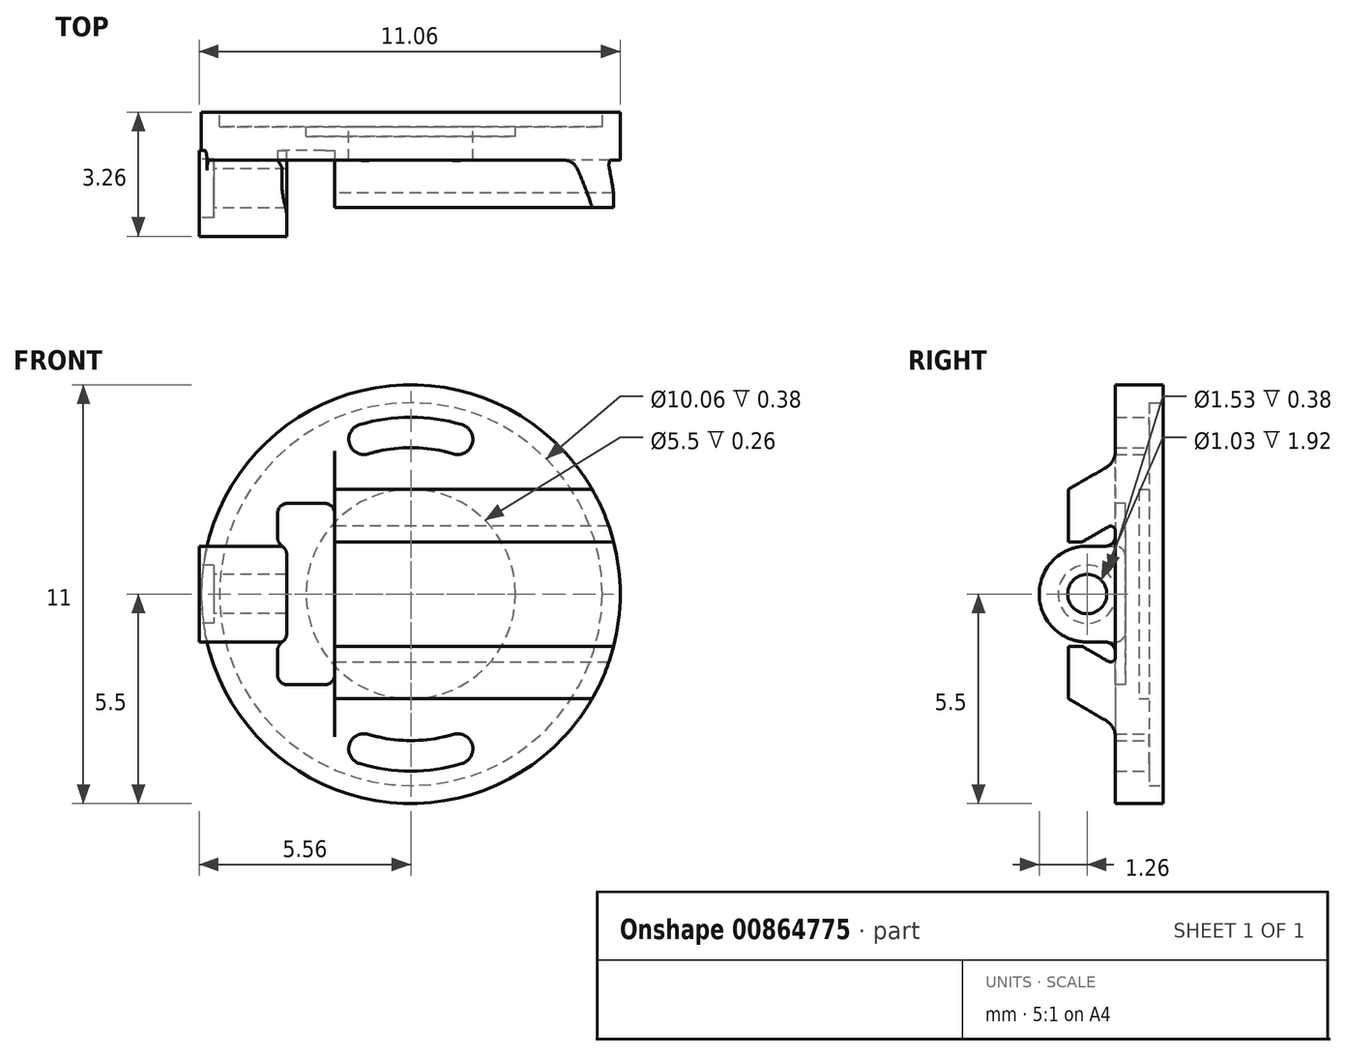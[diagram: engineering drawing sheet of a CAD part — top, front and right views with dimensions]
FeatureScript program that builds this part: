
annotation { "Feature Type Name" : "Feature", "Feature Type Description" : "" }
export const myFeature = defineFeature(function(context is Context, id is Id, definition is map)
    precondition{}
    {
        {
            var Q0;
            Q0=qCreatedBy(makeId("Front.planeOp"),FACE);
            var sketch = newSketch(context, id + "F0", { "sketchPlane" : qUnion([Q0])});
            skCircle(sketch, "E0", {"center": v(0, 0) * mm, "radius": 5.5 * mm});
            skSolve(sketch);
        }
        {
            var Q0;
            Q0 = qSketchRegion(id + "F0", true);
            extrude(context, id + "F1", {"entities" : qUnion([Q0]), "depth" : 1.26 * mm, "offsetDistance" : 25.4 * mm});
        }
        {
            var Q0;
            Q0=makeQuery(id+"F1.opExtrude","CAP_FACE",FACE,{"disambiguationData":[OSD([sQuery(id+"F0.wireOp",EDGE,"E0")])],"isStart":true});
            var sketch = newSketch(context, id + "F2", { "sketchPlane" : qUnion([Q0])});
            skCircle(sketch, "E1", {"center": v(0, 0) * mm, "radius": 5.03 * mm});
            skSolve(sketch);
        }
        {
            var Q0;
            Q0 = qSketchRegion(id + "F2", true);
            extrude(context, id + "F3", {"entities" : qUnion([Q0]), "operationType" : NewBodyOperationType.REMOVE, "oppositeDirection" : true, "depth" : .38 * mm, "offsetDistance" : 25.4 * mm});
        }
        {
            var Q0;
            Q0=makeQuery(id+"F3.boolean.opBoolean","COPY",FACE,{"derivedFrom":makeQuery(id+"F3.opExtrude","CAP_FACE",FACE,{"disambiguationData":[OSD([sQuery(id+"F2.wireOp",EDGE,"E1")])],"isStart":false})});
            var sketch = newSketch(context, id + "F4", { "sketchPlane" : qUnion([Q0])});
            skCircle(sketch, "E2", {"center": v(0, 0) * mm, "radius": 2.75 * mm});
            skSolve(sketch);
        }
        {
            var Q0;
            Q0 = qSketchRegion(id + "F4", true);
            extrude(context, id + "F5", {"entities" : qUnion([Q0]), "operationType" : NewBodyOperationType.REMOVE, "oppositeDirection" : true, "depth" : .26 * mm, "offsetDistance" : 25.4 * mm});
        }
        {
            var Q0;
            Q0=makeQuery(id+"F1.opExtrude","CAP_FACE",FACE,{"disambiguationData":[OSD([sQuery(id+"F0.wireOp",EDGE,"E0")])],"isStart":false});
            var sketch = newSketch(context, id + "F6", { "sketchPlane" : qUnion([Q0])});
            skArc(sketch, "E3", {"start": v(1.23, 4.07) * mm, "mid": v(0, 4.25) * mm, "end": v(-1.23, 4.07) * mm, "construction": true});
            skArc(sketch, "E4", {"start": v(1.11, 3.69) * mm, "mid": v(0, 3.85) * mm, "end": v(-1.11, 3.69) * mm});
            skArc(sketch, "E5", {"start": v(1.35, 4.45) * mm, "mid": v(0, 4.65) * mm, "end": v(-1.35, 4.45) * mm});
            skArc(sketch, "E6", {"start": v(-1.11, -3.69) * mm, "mid": v(0, -3.85) * mm, "end": v(1.11, -3.69) * mm});
            skArc(sketch, "E7", {"start": v(-1.35, -4.45) * mm, "mid": v(0, -4.65) * mm, "end": v(1.35, -4.45) * mm});
            skArc(sketch, "E8.trimOffspring", {"start": v(-1.23, -4.07) * mm, "mid": v(0, -4.25) * mm, "end": v(1.23, -4.07) * mm, "construction": true});
            skArc(sketch, "E9", {"start": v(-1.35, 4.45) * mm, "mid": v(-1.61, 3.95) * mm, "end": v(-1.11, 3.69) * mm});
            skArc(sketch, "E10", {"start": v(1.11, 3.69) * mm, "mid": v(1.61, 3.95) * mm, "end": v(1.35, 4.45) * mm});
            skArc(sketch, "E11", {"start": v(1.35, -4.45) * mm, "mid": v(1.61, -3.95) * mm, "end": v(1.11, -3.69) * mm});
            skArc(sketch, "E12", {"start": v(-1.11, -3.69) * mm, "mid": v(-1.61, -3.95) * mm, "end": v(-1.35, -4.45) * mm});
            skLineSegment(sketch, "E13", {"start": v(0, 0) * mm, "end": v(0, 2.82) * mm, "construction": true});
            skSolve(sketch);
        }
        {
            var Q0;
            Q0 = qSketchRegion(id + "F6", true);
            extrude(context, id + "F7", {"entities" : qUnion([Q0]), "operationType" : NewBodyOperationType.REMOVE, "endBound" : BoundingType.SYMMETRIC, "depth" : 15 * mm, "offsetDistance" : 25.4 * mm});
        }
        {
            var Q0;
            Q0=makeQuery(id+"F1.opExtrude","CAP_FACE",FACE,{"disambiguationData":[OSD([sQuery(id+"F0.wireOp",EDGE,"E0")])],"isStart":false});
            var sketch = newSketch(context, id + "F8", { "sketchPlane" : qUnion([Q0])});
            skLineSegment(sketch, "E14", {"start": v(-2, 2.38) * mm, "end": v(-2, -2.38) * mm});
            skLineSegment(sketch, "E15", {"start": v(-2, -2.38) * mm, "end": v(-3.5, -2.38) * mm});
            skLineSegment(sketch, "E16", {"start": v(-3.5, -2.38) * mm, "end": v(-3.5, -1.48) * mm});
            skLineSegment(sketch, "E17", {"start": v(-3.26, -1.04) * mm, "end": v(-3.26, 1.04) * mm});
            skLineSegment(sketch, "E18", {"start": v(-3.5, 1.48) * mm, "end": v(-3.5, 2.38) * mm});
            skLineSegment(sketch, "E19", {"start": v(-3.5, 2.38) * mm, "end": v(-2, 2.38) * mm});
            skArc(sketch, "E20", {"start": v(-3.26, 1.04) * mm, "mid": v(-3.3, 1.17) * mm, "end": v(-3.38, 1.26) * mm});
            skArc(sketch, "E21", {"start": v(-3.5, 1.48) * mm, "mid": v(-3.47, 1.35) * mm, "end": v(-3.38, 1.26) * mm});
            skArc(sketch, "E22", {"start": v(-3.38, -1.26) * mm, "mid": v(-3.3, -1.17) * mm, "end": v(-3.26, -1.04) * mm});
            skArc(sketch, "E23", {"start": v(-3.38, -1.26) * mm, "mid": v(-3.47, -1.35) * mm, "end": v(-3.5, -1.48) * mm});
            skSolve(sketch);
        }
        {
            var Q0;
            Q0 = qSketchRegion(id + "F8", true);
            extrude(context, id + "F9", {"entities" : qUnion([Q0]), "operationType" : NewBodyOperationType.REMOVE, "oppositeDirection" : true, "depth" : .26 * mm, "offsetDistance" : 25.4 * mm});
        }
        {
            var Q0;
            Q0=makeQuery(id+"F9.boolean.opBoolean","COPY",EDGE,{"derivedFrom":makeQuery(id+"F9.opExtrude","SWEPT_EDGE",EDGE,{"disambiguationData":[OSD([sQuery(id+"F8.wireOp",EDGE,"E14"),sQuery(id+"F8.wireOp",EDGE,"E19")])]})});
            var Q1;
            Q1=makeQuery(id+"F9.boolean.opBoolean","COPY",EDGE,{"derivedFrom":makeQuery(id+"F9.opExtrude","SWEPT_EDGE",EDGE,{"disambiguationData":[OSD([sQuery(id+"F8.wireOp",EDGE,"E18"),sQuery(id+"F8.wireOp",EDGE,"E19")])]})});
            var Q2;
            Q2=makeQuery(id+"F9.boolean.opBoolean","COPY",EDGE,{"derivedFrom":makeQuery(id+"F9.opExtrude","SWEPT_EDGE",EDGE,{"disambiguationData":[OSD([sQuery(id+"F8.wireOp",EDGE,"E15"),sQuery(id+"F8.wireOp",EDGE,"E16")])]})});
            var Q3;
            Q3=makeQuery(id+"F9.boolean.opBoolean","COPY",EDGE,{"derivedFrom":makeQuery(id+"F9.opExtrude","SWEPT_EDGE",EDGE,{"disambiguationData":[OSD([sQuery(id+"F8.wireOp",EDGE,"E14"),sQuery(id+"F8.wireOp",EDGE,"E15")])]})});
            fillet(context, id + "F10", {"entities" : qUnion([Q0, Q1, Q2, Q3]), "radius" : .26 * mm, "tangentPropagation" : true, "allowEdgeOverflow" : false});
        }
        {
            var Q0;
            Q0=makeQuery(id+"F9.boolean.opBoolean","COPY",FACE,{"derivedFrom":makeQuery(id+"F9.opExtrude","SWEPT_FACE",FACE,{"disambiguationData":[OSD([sQuery(id+"F8.wireOp",EDGE,"E17")])]})});
            cPlane(context, id + "F11", {"entities" : qUnion([Q0]), "cplaneType" : CPlaneType.OFFSET, "offset" : 2.3 * mm, "oppositeDirection" : true, "width" : 152.4 * mm, "height" : 152.4 * mm});
        }
        {
            var Q0;
            Q0=qCreatedBy(id+"F11.planeOp",FACE);
            var sketch = newSketch(context, id + "F12", { "sketchPlane" : qUnion([Q0])});
            skLineSegment(sketch, "E24", {"start": v(-1, 1.26) * mm, "end": v(-2, 1.26) * mm});
            skLineSegment(sketch, "E25", {"start": v(-2, -1.26) * mm, "end": v(-1, -1.26) * mm});
            skArc(sketch, "E26", {"start": v(-2, 1.26) * mm, "mid": v(-3.26, 0) * mm, "end": v(-2, -1.26) * mm});
            skLineSegment(sketch, "E27", {"start": v(-1, 1.26) * mm, "end": v(-1, -1.26) * mm});
            skSolve(sketch);
        }
        {
            var Q0;
            {var subQ1=sQuery(id+"F12.wireOp",EDGE,"E24");Q0=makeQuery(id+"F12.imprint","IMPRINT",FACE,{"disambiguationData":[TD([[makeQuery(id+"F12.imprint","IMPRINT",EDGE,{"derivedFrom":subQ1}),1.0]])]});}
            var Q1;
            Q1=makeQuery(id+"F9.boolean.opBoolean","COPY",FACE,{"derivedFrom":makeQuery(id+"F9.opExtrude","SWEPT_FACE",FACE,{"disambiguationData":[OSD([sQuery(id+"F8.wireOp",EDGE,"E17")])]})});
            extrude(context, id + "F13", {"entities" : qUnion([Q0]), "operationType" : NewBodyOperationType.ADD, "endBound" : BoundingType.UP_TO_SURFACE, "depth" : 25.4 * mm, "endBoundEntityFace" : qUnion([Q1]), "offsetDistance" : 25.4 * mm});
        }
        {
            var Q0;
            Q0=makeQuery(id+"F13.opExtrude","CAP_FACE",FACE,{"disambiguationData":[OSD([sQuery(id+"F12.wireOp",EDGE,"E24"),sQuery(id+"F12.wireOp",EDGE,"E25"),sQuery(id+"F12.wireOp",EDGE,"ZlhiLMFL-Lc4S-4lp4-7yYM-Jzgoso8IJn7b"),sQuery(id+"F12.wireOp",EDGE,"E26")])],"isStart":true});
            var sketch = newSketch(context, id + "F14", { "sketchPlane" : qUnion([Q0])});
            skCircle(sketch, "E28", {"center": v(2, 0) * mm, "radius": 0.77 * mm});
            skSolve(sketch);
        }
        {
            var Q0;
            Q0 = qSketchRegion(id + "F14", true);
            extrude(context, id + "F15", {"entities" : qUnion([Q0]), "operationType" : NewBodyOperationType.REMOVE, "oppositeDirection" : true, "depth" : .38 * mm, "offsetDistance" : 25.4 * mm});
        }
        {
            var Q0;
            Q0=makeQuery(id+"F15.boolean.opBoolean","COPY",FACE,{"derivedFrom":makeQuery(id+"F15.opExtrude","CAP_FACE",FACE,{"disambiguationData":[OSD([sQuery(id+"F14.wireOp",EDGE,"E28")])],"isStart":false})});
            var sketch = newSketch(context, id + "F16", { "sketchPlane" : qUnion([Q0])});
            skCircle(sketch, "E29", {"center": v(2, 0) * mm, "radius": 0.52 * mm});
            skSolve(sketch);
        }
        {
            var Q0;
            Q0 = qSketchRegion(id + "F16", true);
            extrude(context, id + "F17", {"entities" : qUnion([Q0]), "operationType" : NewBodyOperationType.REMOVE, "endBound" : BoundingType.THROUGH_ALL, "oppositeDirection" : true, "depth" : 25.4 * mm, "offsetDistance" : 25.4 * mm});
        }
        {
            var Q0;
            Q0=makeQuery(id+"F9.boolean.opBoolean","COPY",FACE,{"derivedFrom":makeQuery(id+"F9.opExtrude","CAP_FACE",FACE,{"disambiguationData":[OSD([sQuery(id+"F8.wireOp",EDGE,"E14"),sQuery(id+"F8.wireOp",EDGE,"E15"),sQuery(id+"F8.wireOp",EDGE,"E16"),sQuery(id+"F8.wireOp",EDGE,"E17"),sQuery(id+"F8.wireOp",EDGE,"E18"),sQuery(id+"F8.wireOp",EDGE,"E19"),sQuery(id+"F8.wireOp",EDGE,"E20"),sQuery(id+"F8.wireOp",EDGE,"E21"),sQuery(id+"F8.wireOp",EDGE,"E22"),sQuery(id+"F8.wireOp",EDGE,"E23")])],"isStart":false})});
            extrude(context, id + "F18", {"entities" : qUnion([Q0]), "operationType" : NewBodyOperationType.REMOVE, "depth" : 1.5 * mm, "offsetDistance" : 25.4 * mm});
        }
        {
            var Q0;
            {var subQ0=sQuery(id+"F12.wireOp",EDGE,"E24");var subQ1=sQuery(id+"F12.wireOp",EDGE,"E27");Q0=makeQuery(id+"F13.boolean.opBoolean","SPLIT",EDGE,{"disambiguationData":[topologyDisambiguationEdgeConnected([makeQuery(id+"F13.opExtrude","SWEPT_FACE",FACE,{"disambiguationData":[OSD([subQ1])]})])],"derivedFrom":makeQuery(id+"F13.opExtrude","SWEPT_EDGE",EDGE,{"disambiguationData":[OSD([subQ0,subQ1])]})});}
            var Q1;
            {var subQ0=sQuery(id+"F12.wireOp",EDGE,"E25");var subQ1=sQuery(id+"F12.wireOp",EDGE,"E27");Q1=makeQuery(id+"F13.boolean.opBoolean","SPLIT",EDGE,{"disambiguationData":[topologyDisambiguationEdgeConnected([makeQuery(id+"F13.opExtrude","SWEPT_FACE",FACE,{"disambiguationData":[OSD([subQ1])]})])],"derivedFrom":makeQuery(id+"F13.opExtrude","SWEPT_EDGE",EDGE,{"disambiguationData":[OSD([subQ0,subQ1])]})});}
            var Q2;
            Q2=makeQuery(id+"F13.boolean.opBoolean","INTERSECT",EDGE,{"derivedFrom":[makeQuery(id+"F1.opExtrude","CAP_FACE",FACE,{"disambiguationData":[OSD([sQuery(id+"F0.wireOp",EDGE,"E0")])],"isStart":false}),makeQuery(id+"F13.opExtrude","SWEPT_FACE",FACE,{"disambiguationData":[OSD([sQuery(id+"F12.wireOp",EDGE,"E24")])]})]});
            var Q3;
            Q3=makeQuery(id+"F13.boolean.opBoolean","INTERSECT",EDGE,{"derivedFrom":[makeQuery(id+"F1.opExtrude","CAP_FACE",FACE,{"disambiguationData":[OSD([sQuery(id+"F0.wireOp",EDGE,"E0")])],"isStart":false}),makeQuery(id+"F13.opExtrude","SWEPT_FACE",FACE,{"disambiguationData":[OSD([sQuery(id+"F12.wireOp",EDGE,"E25")])]})]});
            fillet(context, id + "F19", {"entities" : qUnion([Q0, Q1, Q2, Q3]), "radius" : .26 * mm, "tangentPropagation" : true, "allowEdgeOverflow" : false});
        }
        {
            var Q0;
            Q0=makeQuery(id+"F9.boolean.opBoolean","COPY",FACE,{"derivedFrom":makeQuery(id+"F9.opExtrude","CAP_FACE",FACE,{"disambiguationData":[OSD([sQuery(id+"F8.wireOp",EDGE,"E14"),sQuery(id+"F8.wireOp",EDGE,"E15"),sQuery(id+"F8.wireOp",EDGE,"E16"),sQuery(id+"F8.wireOp",EDGE,"E17"),sQuery(id+"F8.wireOp",EDGE,"E18"),sQuery(id+"F8.wireOp",EDGE,"E19"),sQuery(id+"F8.wireOp",EDGE,"E20"),sQuery(id+"F8.wireOp",EDGE,"E21"),sQuery(id+"F8.wireOp",EDGE,"E22"),sQuery(id+"F8.wireOp",EDGE,"E23")])],"isStart":false})});
            var sketch = newSketch(context, id + "F20", { "sketchPlane" : qUnion([Q0])});
            skLineSegment(sketch, "E30", {"start": v(-2, -2.12) * mm, "end": v(-2, 2.12) * mm});
            skLineSegment(sketch, "E31", {"start": v(-2.26, 2.38) * mm, "end": v(-3.24, 2.38) * mm});
            skLineSegment(sketch, "E32", {"start": v(-3.5, 2.12) * mm, "end": v(-3.5, 1.48) * mm});
            skLineSegment(sketch, "E33", {"start": v(-3.26, -1.04) * mm, "end": v(-3.26, 1.04) * mm});
            skLineSegment(sketch, "E34", {"start": v(-3.5, -1.48) * mm, "end": v(-3.5, -2.12) * mm});
            skLineSegment(sketch, "E35", {"start": v(-3.24, -2.38) * mm, "end": v(-2.26, -2.38) * mm});
            skArc(sketch, "E36", {"start": v(-3.24, 2.38) * mm, "mid": v(-3.42, 2.3) * mm, "end": v(-3.5, 2.12) * mm});
            skArc(sketch, "E37", {"start": v(-2, 2.12) * mm, "mid": v(-2.08, 2.3) * mm, "end": v(-2.26, 2.38) * mm});
            skArc(sketch, "E38", {"start": v(-2.26, -2.38) * mm, "mid": v(-2.08, -2.3) * mm, "end": v(-2, -2.12) * mm});
            skArc(sketch, "E39", {"start": v(-3.5, -2.12) * mm, "mid": v(-3.42, -2.3) * mm, "end": v(-3.24, -2.38) * mm});
            skArc(sketch, "E40", {"start": v(-3.5, 1.48) * mm, "mid": v(-3.47, 1.35) * mm, "end": v(-3.38, 1.26) * mm});
            skArc(sketch, "E41", {"start": v(-3.26, 1.04) * mm, "mid": v(-3.3, 1.17) * mm, "end": v(-3.38, 1.26) * mm});
            skArc(sketch, "E42", {"start": v(-3.38, -1.26) * mm, "mid": v(-3.3, -1.17) * mm, "end": v(-3.26, -1.04) * mm});
            skArc(sketch, "E43", {"start": v(-3.38, -1.26) * mm, "mid": v(-3.47, -1.35) * mm, "end": v(-3.5, -1.48) * mm});
            skSolve(sketch);
        }
        {
            var Q0;
            Q0 = qSketchRegion(id + "F20", true);
            extrude(context, id + "F21", {"entities" : qUnion([Q0]), "operationType" : NewBodyOperationType.REMOVE, "depth" : 15 * mm, "offsetDistance" : 25.4 * mm});
        }
        {
            var Q0;
            Q0=makeQuery(id+"F9.boolean.opBoolean","COPY",FACE,{"derivedFrom":makeQuery(id+"F9.opExtrude","SWEPT_FACE",FACE,{"disambiguationData":[OSD([sQuery(id+"F8.wireOp",EDGE,"E14")])]})});
            var sketch = newSketch(context, id + "F22", { "sketchPlane" : qUnion([Q0])});
            skLineSegment(sketch, "E44", {"start": v(1.5, 3.32) * mm, "end": v(2.5, 2.75) * mm});
            skLineSegment(sketch, "E45", {"start": v(2.5, 2.75) * mm, "end": v(2.5, 1.37) * mm});
            skLineSegment(sketch, "E46", {"start": v(1.5, -3.32) * mm, "end": v(2.5, -2.75) * mm});
            skLineSegment(sketch, "E47", {"start": v(2.5, -2.75) * mm, "end": v(2.5, -1.38) * mm});
            skLineSegment(sketch, "E48", {"start": v(1.44, 1.77) * mm, "end": v(2.13, 1.37) * mm});
            skLineSegment(sketch, "E49", {"start": v(2.13, 1.38) * mm, "end": v(2.5, 1.38) * mm});
            skLineSegment(sketch, "E50", {"start": v(1.44, -1.77) * mm, "end": v(2.13, -1.38) * mm});
            skLineSegment(sketch, "E51", {"start": v(2.13, -1.38) * mm, "end": v(2.5, -1.38) * mm});
            skArc(sketch, "E52", {"start": v(1.26, 3.75) * mm, "mid": v(1.33, 3.5) * mm, "end": v(1.5, 3.32) * mm});
            skArc(sketch, "E53", {"start": v(1.5, -3.32) * mm, "mid": v(1.33, -3.5) * mm, "end": v(1.26, -3.75) * mm});
            skLineSegment(sketch, "E54", {"start": v(1.26, 1.87) * mm, "end": v(1.26, 3.75) * mm});
            skLineSegment(sketch, "E55", {"start": v(1.26, -1.88) * mm, "end": v(1.26, -3.75) * mm});
            skArc(sketch, "E56", {"start": v(1.44, 1.77) * mm, "mid": v(1.32, 1.77) * mm, "end": v(1.26, 1.67) * mm});
            skArc(sketch, "E57", {"start": v(1.26, -1.67) * mm, "mid": v(1.32, -1.77) * mm, "end": v(1.44, -1.77) * mm});
            skLineSegment(sketch, "E58", {"start": v(1.26, -1.88) * mm, "end": v(1.26, -1.67) * mm});
            skLineSegment(sketch, "E59", {"start": v(1.26, 1.87) * mm, "end": v(1.26, 1.67) * mm});
            skSolve(sketch);
        }
        {
            var Q0;
            Q0 = qSketchRegion(id + "F22", true);
            var Q1;
            Q1=makeQuery(id+"F1.opExtrude","SWEPT_FACE",FACE,{"disambiguationData":[OSD([sQuery(id+"F0.wireOp",EDGE,"E0")])]});
            extrude(context, id + "F23", {"entities" : qUnion([Q0]), "operationType" : NewBodyOperationType.ADD, "endBound" : BoundingType.UP_TO_SURFACE, "oppositeDirection" : true, "depth" : 25.4 * mm, "endBoundEntityFace" : qUnion([Q1]), "offsetDistance" : 25.4 * mm});
        }
        {
            var Q0;
            Q0=makeQuery(id+"F3.boolean.opBoolean","COPY",FACE,{"derivedFrom":makeQuery(id+"F3.opExtrude","CAP_FACE",FACE,{"disambiguationData":[OSD([sQuery(id+"F2.wireOp",EDGE,"E1")])],"isStart":false})});
            var sketch = newSketch(context, id + "F24", { "sketchPlane" : qUnion([Q0])});
            skArc(sketch, "E60", {"start": v(-1.35, -4.45) * mm, "mid": v(0, -4.65) * mm, "end": v(1.35, -4.45) * mm});
            skArc(sketch, "E61", {"start": v(-1.11, -3.69) * mm, "mid": v(0, -3.85) * mm, "end": v(1.11, -3.69) * mm});
            skArc(sketch, "E62", {"start": v(1.35, -4.45) * mm, "mid": v(1.61, -3.95) * mm, "end": v(1.11, -3.69) * mm});
            skArc(sketch, "E63", {"start": v(-1.11, -3.69) * mm, "mid": v(-1.61, -3.95) * mm, "end": v(-1.35, -4.45) * mm});
            skArc(sketch, "E64", {"start": v(1.11, 3.69) * mm, "mid": v(0, 3.85) * mm, "end": v(-1.11, 3.69) * mm});
            skArc(sketch, "E65", {"start": v(1.35, 4.45) * mm, "mid": v(0, 4.65) * mm, "end": v(-1.35, 4.45) * mm});
            skArc(sketch, "E66", {"start": v(1.11, 3.69) * mm, "mid": v(1.61, 3.95) * mm, "end": v(1.35, 4.45) * mm});
            skArc(sketch, "E67", {"start": v(-1.35, 4.45) * mm, "mid": v(-1.61, 3.95) * mm, "end": v(-1.11, 3.69) * mm});
            skSolve(sketch);
        }
        {
            var Q0;
            Q0 = qSketchRegion(id + "F24", true);
            extrude(context, id + "F25", {"entities" : qUnion([Q0]), "operationType" : NewBodyOperationType.REMOVE, "oppositeDirection" : true, "depth" : 10 * mm, "offsetDistance" : 25.4 * mm});
        }
    });
